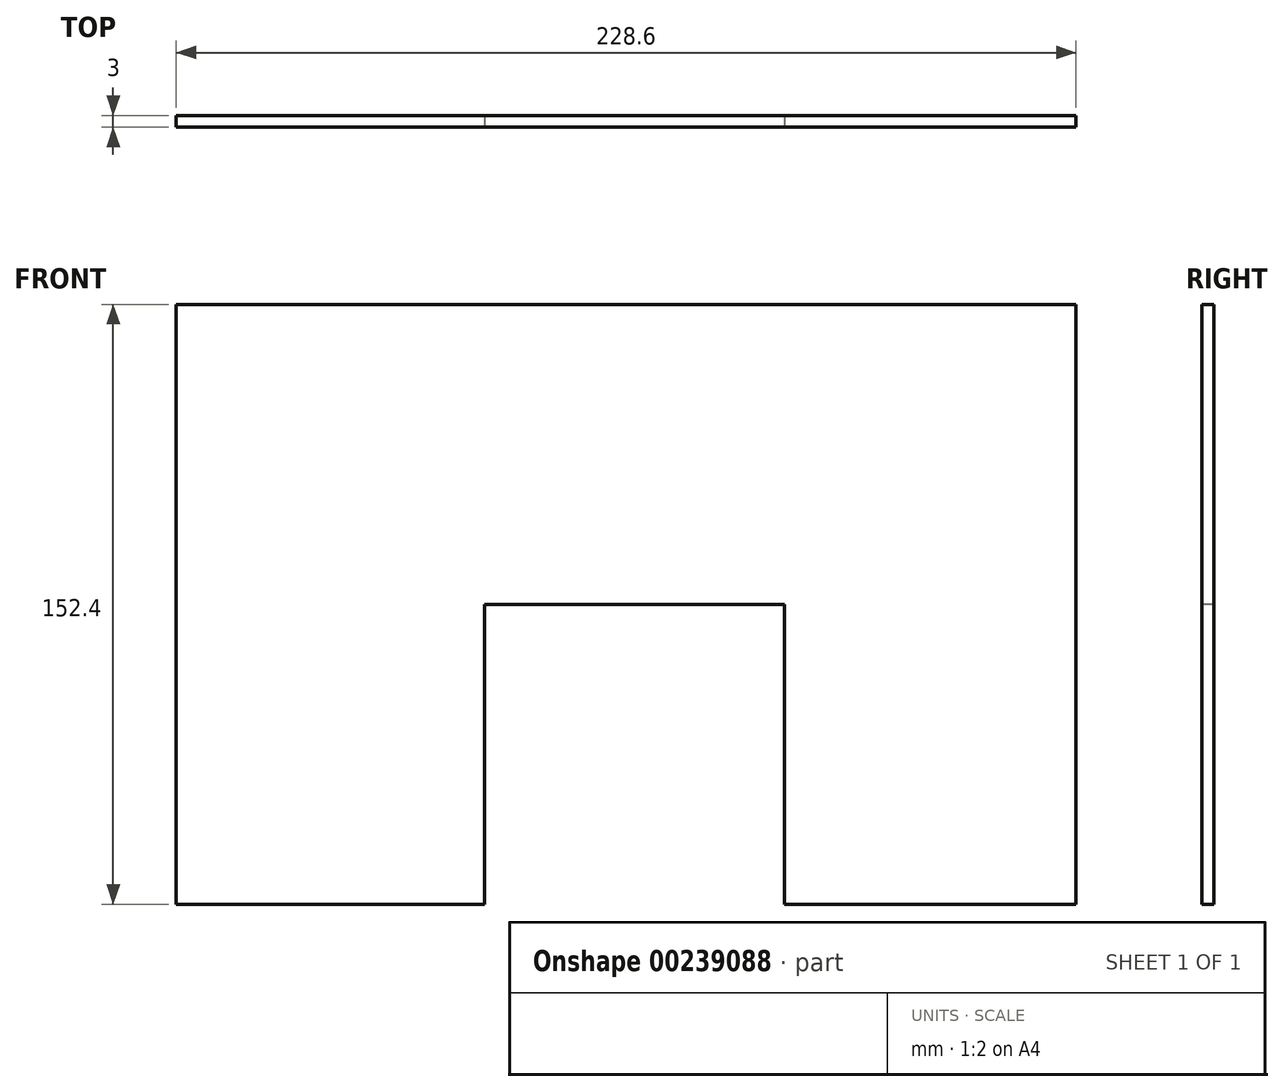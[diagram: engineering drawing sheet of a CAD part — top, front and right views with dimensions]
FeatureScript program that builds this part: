
annotation { "Feature Type Name" : "Feature", "Feature Type Description" : "" }
export const myFeature = defineFeature(function(context is Context, id is Id, definition is map)
    precondition{}
    {
        {
            assignVariable(context, id + "F0", {"name" : "v", "anyValue" : 3});
        }
        {
            var Q0;
            Q0=qCreatedBy(makeId("Front.planeOp"),FACE);
            var sketch = newSketch(context, id + "F1", { "sketchPlane" : qUnion([Q0])});
            skLineSegment(sketch, "E0.bottom", {"start": v(-114.3, 76.2) * mm, "end": v(114.3, 76.2) * mm});
            skLineSegment(sketch, "E0.top", {"start": v(-114.3, -76.2) * mm, "end": v(114.3, -76.2) * mm});
            skLineSegment(sketch, "E0.left", {"start": v(-114.3, 76.2) * mm, "end": v(-114.3, -76.2) * mm});
            skLineSegment(sketch, "E0.right", {"start": v(114.3, 76.2) * mm, "end": v(114.3, -76.2) * mm});
            skPoint(sketch, "E0.middle", {"position": v(0, 0) * mm});
            skSolve(sketch);
        }
        {
            var Q0;
            Q0 = qSketchRegion(id + "F1", true);
            extrude(context, id + "F2", {"entities" : qUnion([Q0]), "depth" : (getVariable(context, 'v')) * mm});
        }
        {
            var Q0;
            Q0=makeQuery(id+"F2.opExtrude","CAP_FACE",FACE,{"disambiguationData":[OSD([sQuery(id+"F1.wireOp",EDGE,"E0.bottom"),sQuery(id+"F1.wireOp",EDGE,"E0.top"),sQuery(id+"F1.wireOp",EDGE,"E0.left"),sQuery(id+"F1.wireOp",EDGE,"E0.right")])],"isStart":false});
            var sketch = newSketch(context, id + "F3", { "sketchPlane" : qUnion([Q0])});
            skLineSegment(sketch, "E1.bottom", {"start": v(-36.04, -76.2) * mm, "end": v(40.16, -76.2) * mm});
            skLineSegment(sketch, "E1.top", {"start": v(-36.04, 0) * mm, "end": v(40.16, 0) * mm});
            skLineSegment(sketch, "E1.left", {"start": v(-36.04, -76.2) * mm, "end": v(-36.04, 0) * mm});
            skLineSegment(sketch, "E1.right", {"start": v(40.16, -76.2) * mm, "end": v(40.16, 0) * mm});
            skSolve(sketch);
        }
        {
            var Q0;
            Q0 = qSketchRegion(id + "F3", true);
            extrude(context, id + "F4", {"entities" : qUnion([Q0]), "operationType" : NewBodyOperationType.REMOVE, "endBound" : BoundingType.THROUGH_ALL, "oppositeDirection" : true, "depth" : (getVariable(context, 'v')) * mm});
        }
    });
